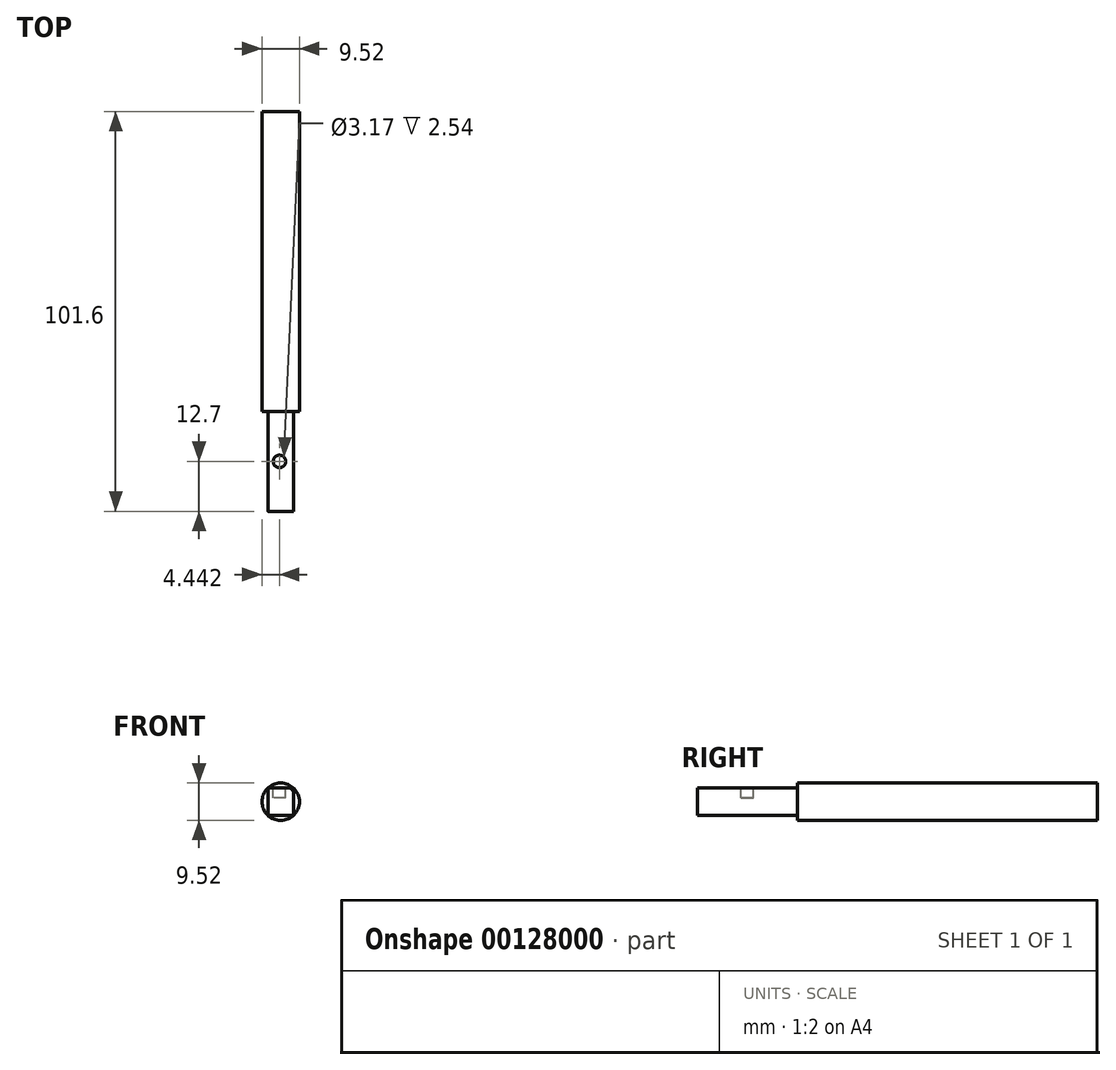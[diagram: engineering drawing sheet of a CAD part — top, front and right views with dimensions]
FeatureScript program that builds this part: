
annotation { "Feature Type Name" : "Feature", "Feature Type Description" : "" }
export const myFeature = defineFeature(function(context is Context, id is Id, definition is map)
    precondition{}
    {
        {
            var Q0;
            Q0=qCreatedBy(makeId("Front.planeOp"),FACE);
            var sketch = newSketch(context, id + "F0", { "sketchPlane" : qUnion([Q0])});
            skCircle(sketch, "E0", {"center": v(0, 0) * mm, "radius": 4.76 * mm});
            skSolve(sketch);
        }
        {
            var Q0;
            Q0 = qSketchRegion(id + "F0", true);
            extrude(context, id + "F1", {"entities" : qUnion([Q0]), "depth" : 101.6 * mm});
        }
        {
            var Q0;
            Q0=makeQuery(id+"F1.opExtrude","CAP_FACE",FACE,{"disambiguationData":[OSD([sQuery(id+"F0.wireOp",EDGE,"E0")])],"isStart":false});
            var sketch = newSketch(context, id + "F2", { "sketchPlane" : qUnion([Q0])});
            skLineSegment(sketch, "E1.bottom", {"start": v(-2.6, 3.5) * mm, "end": v(1.97, 3.5) * mm});
            skLineSegment(sketch, "E1.top", {"start": v(-2.6, -3.5) * mm, "end": v(2.6, -3.5) * mm});
            skLineSegment(sketch, "E1.left", {"start": v(-3.24, 2.86) * mm, "end": v(-3.24, -2.86) * mm});
            skLineSegment(sketch, "E1.right", {"start": v(3.24, 2.22) * mm, "end": v(3.24, -2.86) * mm});
            skPoint(sketch, "E1.middle", {"position": v(0, 0) * mm});
            skCircle(sketch, "E2", {"center": v(0, 0) * mm, "radius": 4.76 * mm});
            skPoint(sketch, "E3.visualSharp", {"position": v(-3.24, 3.5) * mm});
            skArc(sketch, "E3.filletArc", {"start": v(-2.6, 3.5) * mm, "mid": v(-3.05, 3.3) * mm, "end": v(-3.24, 2.86) * mm});
            skPoint(sketch, "E4.visualSharp", {"position": v(3.24, 3.5) * mm});
            skArc(sketch, "E4.filletArc", {"start": v(3.24, 2.22) * mm, "mid": v(2.87, 3.12) * mm, "end": v(1.97, 3.5) * mm});
            skPoint(sketch, "E5.visualSharp", {"position": v(-3.24, -3.5) * mm});
            skArc(sketch, "E5.filletArc", {"start": v(-3.24, -2.86) * mm, "mid": v(-3.05, -3.3) * mm, "end": v(-2.6, -3.5) * mm});
            skPoint(sketch, "E6.visualSharp", {"position": v(3.24, -3.5) * mm});
            skArc(sketch, "E6.filletArc", {"start": v(2.6, -3.5) * mm, "mid": v(3.05, -3.3) * mm, "end": v(3.24, -2.86) * mm});
            skSolve(sketch);
        }
        {
            var Q0;
            Q0=makeQuery(id+"F2.imprint","IMPRINT",FACE,{"disambiguationData":[TD([[makeQuery(id+"F2.imprint","IMPRINT",EDGE,{"derivedFrom":sQuery(id+"F2.wireOp",EDGE,"E1.bottom")}),1.0]])]});
            extrude(context, id + "F3", {"entities" : qUnion([Q0]), "operationType" : NewBodyOperationType.REMOVE, "oppositeDirection" : true, "depth" : 25.4 * mm});
        }
        {
            var Q0;
            Q0=makeQuery(id+"F3.boolean.opBoolean","COPY",FACE,{"derivedFrom":makeQuery(id+"F3.opExtrude","SWEPT_FACE",FACE,{"disambiguationData":[OSD([sQuery(id+"F2.wireOp",EDGE,"E1.bottom")])]})});
            var sketch = newSketch(context, id + "F4", { "sketchPlane" : qUnion([Q0])});
            skLineSegment(sketch, "E7", {"start": v(-0.32, -101.6) * mm, "end": v(-0.32, -88.9) * mm});
            skCircle(sketch, "E8", {"center": v(-0.32, -88.9) * mm, "radius": 1.59 * mm});
            skSolve(sketch);
        }
        {
            var Q0;
            Q0 = qSketchRegion(id + "F4", true);
            extrude(context, id + "F5", {"entities" : qUnion([Q0]), "operationType" : NewBodyOperationType.REMOVE, "oppositeDirection" : true, "depth" : 2.54 * mm});
        }
    });
